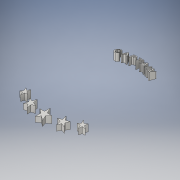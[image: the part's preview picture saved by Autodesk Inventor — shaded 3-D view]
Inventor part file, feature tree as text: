
AUTODESK INVENTOR PART (.ipt)
format: ipt  version: 2016 (Build 200138000, 138)  size: 487,424 bytes
history: native  units: in
note: dims shown in document units (in); Inventor stores cm internally (conversion verified against a paired STEP export)
features: sketch x2, revolve x1, extrude x1, projected_geometry x1
ambient origin geometry x8: Origin, YZ Plane, XZ Plane, XY Plane, X Axis, Y Axis, Z Axis, Center Point
bodies: Solid1 (feature_tree)
feature tree (5):
  revolve  "Revolution1"  [1 undecoded]
  extrude  "Extrusion1"  Depth=0.1in
  sketch  "Sketch1"  dims[d0=0.8265in d1=0.175in]
  sketch  "Sketch2"  dims[d2=0.05in d3=0.1in d4=0.15in d5=0.275in d6=90.0deg d7=0.075in d10=0.245in d11=0.1374in d12=0.1202in d13=1.95in d14=0.089in d15=0.074in d16=0.059in d17=0.0in d18=0.0in d19=0.074in d20=0.059in]
  projected_geometry  "Projected Loop1"
note: 1 required parameter value undecoded (feature->parameter linkage not recoverable at this tier; creation-order binding heuristic only, values carry confidence <= 0.55)
